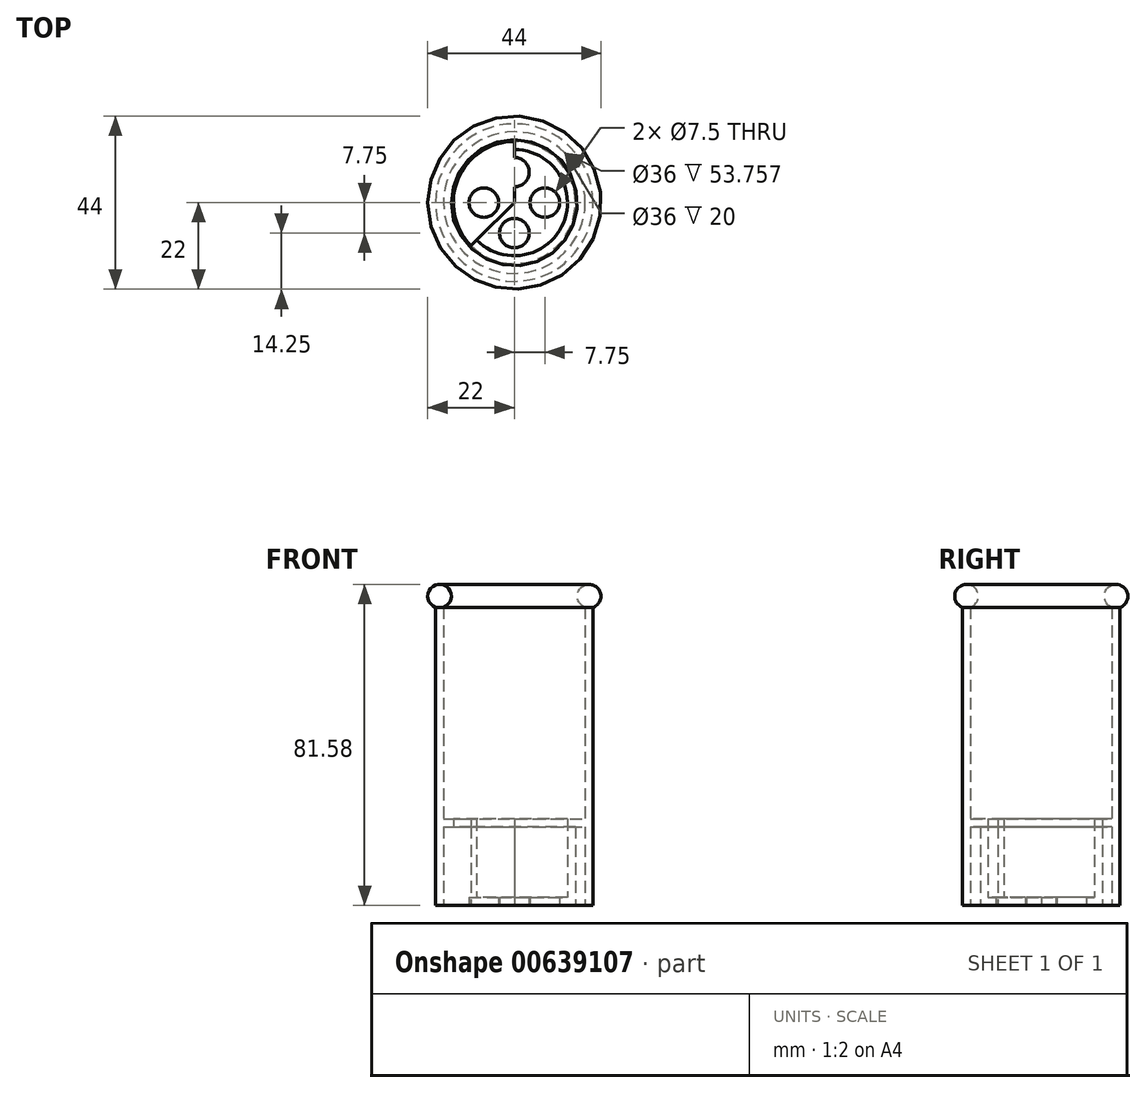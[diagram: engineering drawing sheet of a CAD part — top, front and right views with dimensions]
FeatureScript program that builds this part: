
annotation { "Feature Type Name" : "Feature", "Feature Type Description" : "" }
export const myFeature = defineFeature(function(context is Context, id is Id, definition is map)
    precondition{}
    {
        {
            var Q0;
            Q0=qCreatedBy(makeId("Front.planeOp"),FACE);
            var sketch = newSketch(context, id + "F0", { "sketchPlane" : qUnion([Q0])});
            skLineSegment(sketch, "E0.bottom", {"start": v(0, 0) * mm, "end": v(20, 0) * mm});
            skLineSegment(sketch, "E0.top", {"start": v(0, 58.58) * mm, "end": v(20, 58.58) * mm});
            skLineSegment(sketch, "E0.left", {"start": v(0, 0) * mm, "end": v(0, 58.58) * mm});
            skLineSegment(sketch, "E0.right", {"start": v(20, 0) * mm, "end": v(20, 58.58) * mm});
            skLineSegment(sketch, "E1.bottom", {"start": v(18, 0) * mm, "end": v(20, 0) * mm});
            skLineSegment(sketch, "E1.top", {"start": v(18, 58.58) * mm, "end": v(20, 58.58) * mm});
            skLineSegment(sketch, "E1.right", {"start": v(18, 0) * mm, "end": v(18, 58.58) * mm});
            skLineSegment(sketch, "E2.bottom", {"start": v(20, 0) * mm, "end": v(18, 0) * mm});
            skLineSegment(sketch, "E2.top", {"start": v(20, -20) * mm, "end": v(18, -20) * mm});
            skLineSegment(sketch, "E2.left", {"start": v(20, 0) * mm, "end": v(20, -20) * mm});
            skLineSegment(sketch, "E2.right", {"start": v(18, 0) * mm, "end": v(18, -20) * mm});
            skLineSegment(sketch, "E3.bottom", {"start": v(0, 0) * mm, "end": v(15.5, 0) * mm});
            skLineSegment(sketch, "E3.top", {"start": v(0, -20) * mm, "end": v(15.5, -20) * mm});
            skLineSegment(sketch, "E3.left", {"start": v(0, 0) * mm, "end": v(0, -20) * mm});
            skLineSegment(sketch, "E3.right", {"start": v(15.5, 0) * mm, "end": v(15.5, -20) * mm});
            skLineSegment(sketch, "E4.0", {"start": v(13.5, 0) * mm, "end": v(13.5, -18) * mm});
            skLineSegment(sketch, "E4.1", {"start": v(0, -18) * mm, "end": v(13.5, -18) * mm});
            skPoint(sketch, "E5", {"position": v(19, 58.58) * mm});
            skCircle(sketch, "E6", {"center": v(19, 58.58) * mm, "radius": 3 * mm});
            skLineSegment(sketch, "E7.bottom", {"start": v(20, 0) * mm, "end": v(13.5, 0) * mm});
            skLineSegment(sketch, "E7.top", {"start": v(20, 2) * mm, "end": v(13.5, 2) * mm});
            skLineSegment(sketch, "E7.left", {"start": v(20, 0) * mm, "end": v(20, 2) * mm});
            skLineSegment(sketch, "E7.right", {"start": v(13.5, 0) * mm, "end": v(13.5, 2) * mm});
            skSolve(sketch);
        }
        {
            var Q0;
            {var subQ0=sQuery(id+"F0.wireOp",EDGE,"E0.top");var subQ1=makeQuery(id+"F0.imprint","INTERSECT",VERTEX,{"derivedFrom":[subQ0,sQuery(id+"F0.wireOp",EDGE,"E1.right")]});Q0=makeQuery(id+"F0.imprint","IMPRINT",FACE,{"disambiguationData":[TD([[makeQuery(id+"F0.imprint","IMPRINT",EDGE,{"disambiguationData":[TD([[subQ1,-1.0]])],"derivedFrom":subQ0}),1.0]])]});}
            var Q1;
            {var subQ0=sQuery(id+"F0.wireOp",EDGE,"E1.right");var subQ1=sQuery(id+"F0.wireOp",EDGE,"E0.top");var subQ2=makeQuery(id+"F0.imprint","INTERSECT",VERTEX,{"derivedFrom":[subQ1,subQ0]});Q1=makeQuery(id+"F0.imprint","IMPRINT",FACE,{"disambiguationData":[TD([[makeQuery(id+"F0.imprint","IMPRINT",EDGE,{"disambiguationData":[TD([[subQ2,-1.0]])],"derivedFrom":subQ1}),-1.0]])]});}
            var Q2;
            {var subQ0=sQuery(id+"F0.wireOp",EDGE,"E1.right");var subQ1=sQuery(id+"F0.wireOp",EDGE,"E0.top");var subQ2=makeQuery(id+"F0.imprint","INTERSECT",VERTEX,{"derivedFrom":[subQ1,subQ0]});Q2=makeQuery(id+"F0.imprint","IMPRINT",FACE,{"disambiguationData":[TD([[makeQuery(id+"F0.imprint","IMPRINT",EDGE,{"disambiguationData":[TD([[subQ2,1.0]])],"derivedFrom":subQ1}),-1.0]])]});}
            var Q3;
            {var subQ2=sQuery(id+"F0.wireOp",EDGE,"E3.top");Q3=makeQuery(id+"F0.imprint","IMPRINT",FACE,{"disambiguationData":[TD([[makeQuery(id+"F0.imprint","IMPRINT",EDGE,{"derivedFrom":subQ2}),1.0]])]});}
            var Q4;
            {var subQ0=sQuery(id+"F0.wireOp",EDGE,"E0.right");var subQ5=sQuery(id+"F0.wireOp",EDGE,"E7.top");var subQ6=makeQuery(id+"F0.imprint","INTERSECT",VERTEX,{"derivedFrom":[subQ0,subQ5]});Q4=makeQuery(id+"F0.imprint","IMPRINT",FACE,{"disambiguationData":[TD([[makeQuery(id+"F0.imprint","IMPRINT",EDGE,{"disambiguationData":[TD([[subQ6,-1.0]])],"derivedFrom":subQ5}),1.0]])]});}
            var Q5;
            {var subQ6=sQuery(id+"F0.wireOp",EDGE,"E7.right");Q5=makeQuery(id+"F0.imprint","IMPRINT",FACE,{"disambiguationData":[TD([[makeQuery(id+"F0.imprint","IMPRINT",EDGE,{"derivedFrom":subQ6}),-1.0]])]});}
            var Q6;
            Q6=makeQuery(id+"F0.imprint","IMPRINT",FACE,{"disambiguationData":[TD([[makeQuery(id+"F0.imprint","IMPRINT",EDGE,{"derivedFrom":sQuery(id+"F0.wireOp",EDGE,"E2.top")}),-1.0]])]});
            var Q7;
            {var subQ0=sQuery(id+"F0.wireOp",EDGE,"E7.top");var subQ1=sQuery(id+"F0.wireOp",EDGE,"E0.right");var subQ2=makeQuery(id+"F0.imprint","INTERSECT",VERTEX,{"derivedFrom":[subQ1,subQ0]});Q7=makeQuery(id+"F0.imprint","IMPRINT",FACE,{"disambiguationData":[TD([[makeQuery(id+"F0.imprint","IMPRINT",EDGE,{"disambiguationData":[TD([[subQ2,-1.0]])],"derivedFrom":subQ1}),1.0]])]});}
            var Q8;
            Q8=sQuery(id+"F0.wireOp",EDGE,"E0.left");
            revolve(context, id + "F1", {"entities" : qUnion([Q0, Q1, Q2, Q3, Q4, Q5, Q6, Q7]), "axis" : qUnion([Q8]), "revolveType" : RevolveType.FULL});
        }
        {
            var Q0;
            Q0=makeQuery(id+"F1.opRevolve","SWEPT_FACE",FACE,{"disambiguationData":[OSD([sQuery(id+"F0.wireOp",EDGE,"E3.top")])]});
            var sketch = newSketch(context, id + "F2", { "sketchPlane" : qUnion([Q0])});
            skPoint(sketch, "E8.0", {"position": v(0, 0) * mm});
            skCircle(sketch, "E9.0", {"center": v(0, 0) * mm, "radius": 15.5 * mm});
            skLineSegment(sketch, "E10", {"start": v(0, 0) * mm, "end": v(15.5, 0) * mm});
            skCircle(sketch, "E11", {"center": v(7.75, 0) * mm, "radius": 3.75 * mm});
            skLineSegment(sketch, "E12", {"start": v(0, 15.5) * mm, "end": v(0, -15.5) * mm});
            skCircle(sketch, "E13.MirrorC", {"center": v(-7.75, 0) * mm, "radius": 3.75 * mm});
            skLineSegment(sketch, "E14", {"start": v(0, 0) * mm, "end": v(-10.96, 10.96) * mm});
            skCircle(sketch, "E15.MirrorC", {"center": v(0, 7.75) * mm, "radius": 3.75 * mm});
            skCircle(sketch, "E16.MirrorC", {"center": v(0, -7.75) * mm, "radius": 3.75 * mm});
            skSolve(sketch);
        }
        {
            var Q0;
            {var subQ0=sQuery(id+"F2.wireOp",EDGE,"E16.MirrorC");var subQ1=sQuery(id+"F2.wireOp",EDGE,"E12");var subQ2=makeQuery(id+"F2.imprint","INTERSECT",VERTEX,{"disambiguationData":[OD(0.0)],"derivedFrom":[subQ1,subQ0]});Q0=makeQuery(id+"F2.imprint","IMPRINT",FACE,{"disambiguationData":[TD([[makeQuery(id+"F2.imprint","IMPRINT",EDGE,{"disambiguationData":[TD([[subQ2,-1.0]])],"derivedFrom":subQ1}),1.0]])]});}
            var Q1;
            {var subQ0=sQuery(id+"F2.wireOp",EDGE,"E16.MirrorC");var subQ1=sQuery(id+"F2.wireOp",EDGE,"E12");var subQ2=makeQuery(id+"F2.imprint","INTERSECT",VERTEX,{"disambiguationData":[OD(0.0)],"derivedFrom":[subQ1,subQ0]});Q1=makeQuery(id+"F2.imprint","IMPRINT",FACE,{"disambiguationData":[TD([[makeQuery(id+"F2.imprint","IMPRINT",EDGE,{"disambiguationData":[TD([[subQ2,-1.0]])],"derivedFrom":subQ1}),-1.0]])]});}
            var Q2;
            Q2=makeQuery(id+"F2.imprint","IMPRINT",FACE,{"disambiguationData":[TD([[makeQuery(id+"F2.imprint","IMPRINT",EDGE,{"derivedFrom":sQuery(id+"F2.wireOp",EDGE,"E13.MirrorC")}),-1.0]])]});
            var Q3;
            {var subQ0=sQuery(id+"F2.wireOp",EDGE,"E15.MirrorC");var subQ1=sQuery(id+"F2.wireOp",EDGE,"E12");var subQ2=makeQuery(id+"F2.imprint","INTERSECT",VERTEX,{"disambiguationData":[OD(0.0)],"derivedFrom":[subQ1,subQ0]});Q3=makeQuery(id+"F2.imprint","IMPRINT",FACE,{"disambiguationData":[TD([[makeQuery(id+"F2.imprint","IMPRINT",EDGE,{"disambiguationData":[TD([[subQ2,-1.0]])],"derivedFrom":subQ1}),1.0]])]});}
            var Q4;
            {var subQ0=sQuery(id+"F2.wireOp",EDGE,"E15.MirrorC");var subQ1=sQuery(id+"F2.wireOp",EDGE,"E12");var subQ2=makeQuery(id+"F2.imprint","INTERSECT",VERTEX,{"disambiguationData":[OD(0.0)],"derivedFrom":[subQ1,subQ0]});Q4=makeQuery(id+"F2.imprint","IMPRINT",FACE,{"disambiguationData":[TD([[makeQuery(id+"F2.imprint","IMPRINT",EDGE,{"disambiguationData":[TD([[subQ2,-1.0]])],"derivedFrom":subQ1}),-1.0]])]});}
            var Q5;
            {var subQ0=sQuery(id+"F2.wireOp",EDGE,"E11");var subQ1=sQuery(id+"F2.wireOp",EDGE,"E10");var subQ2=makeQuery(id+"F2.imprint","INTERSECT",VERTEX,{"disambiguationData":[OD(0.0)],"derivedFrom":[subQ1,subQ0]});Q5=makeQuery(id+"F2.imprint","IMPRINT",FACE,{"disambiguationData":[TD([[makeQuery(id+"F2.imprint","IMPRINT",EDGE,{"disambiguationData":[TD([[subQ2,-1.0]])],"derivedFrom":subQ1}),1.0]])]});}
            var Q6;
            {var subQ0=sQuery(id+"F2.wireOp",EDGE,"E11");var subQ1=sQuery(id+"F2.wireOp",EDGE,"E10");var subQ2=makeQuery(id+"F2.imprint","INTERSECT",VERTEX,{"disambiguationData":[OD(0.0)],"derivedFrom":[subQ1,subQ0]});Q6=makeQuery(id+"F2.imprint","IMPRINT",FACE,{"disambiguationData":[TD([[makeQuery(id+"F2.imprint","IMPRINT",EDGE,{"disambiguationData":[TD([[subQ2,-1.0]])],"derivedFrom":subQ1}),-1.0]])]});}
            extrude(context, id + "F3", {"entities" : qUnion([Q0, Q1, Q2, Q3, Q4, Q5, Q6]), "operationType" : NewBodyOperationType.REMOVE, "oppositeDirection" : true, "depth" : 25.4 * mm, "offsetDistance" : 25.4 * mm});
        }
    });
